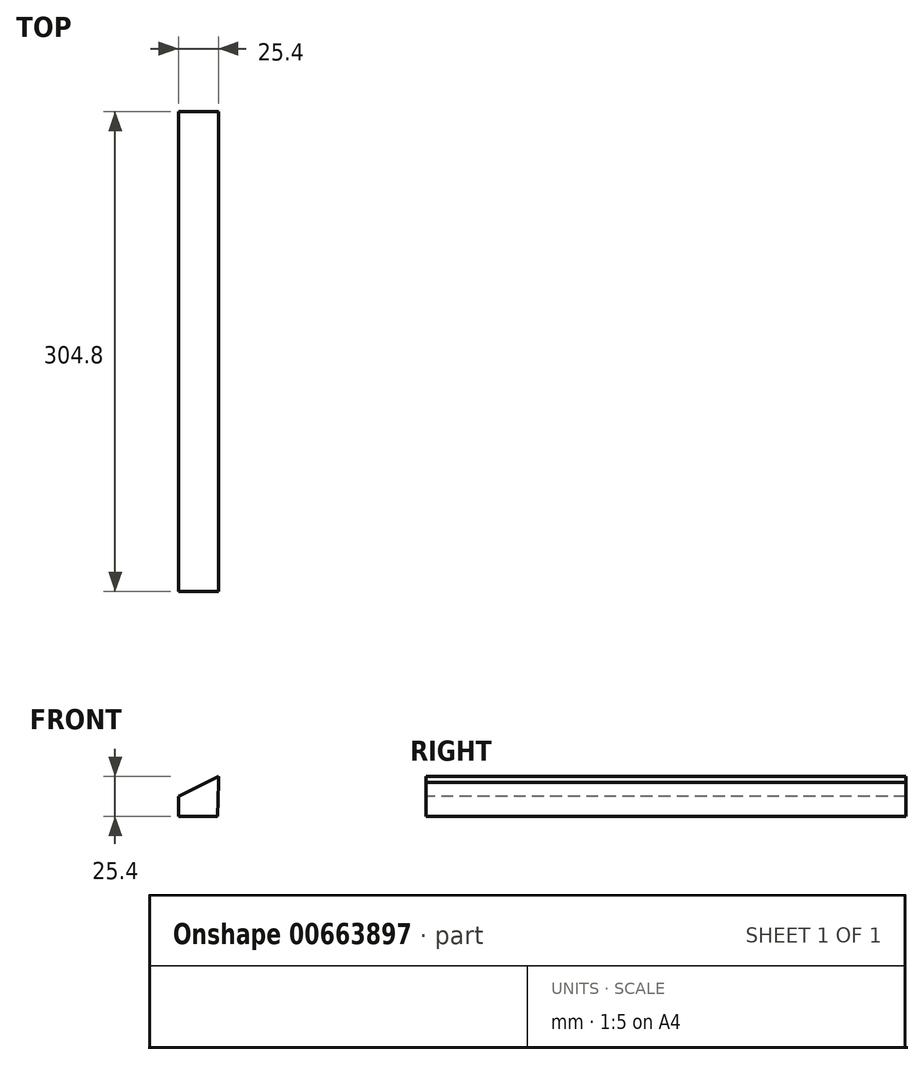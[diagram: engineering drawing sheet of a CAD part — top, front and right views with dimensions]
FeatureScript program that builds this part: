
annotation { "Feature Type Name" : "Feature", "Feature Type Description" : "" }
export const myFeature = defineFeature(function(context is Context, id is Id, definition is map)
    precondition{}
    {
        {
            var Q0;
            Q0=qCreatedBy(makeId("Front.planeOp"),FACE);
            var sketch = newSketch(context, id + "F0", { "sketchPlane" : qUnion([Q0])});
            skLineSegment(sketch, "E0.bottom", {"start": v(-12.7, 12.7) * mm, "end": v(12.7, 12.7) * mm});
            skLineSegment(sketch, "E0.top", {"start": v(-12.7, -12.7) * mm, "end": v(12.7, -12.7) * mm});
            skLineSegment(sketch, "E0.left", {"start": v(-12.7, 12.7) * mm, "end": v(-12.7, -12.7) * mm});
            skLineSegment(sketch, "E0.right", {"start": v(12.7, 12.7) * mm, "end": v(12.7, -12.7) * mm});
            skSolve(sketch);
        }
        {
            var Q0;
            Q0 = qSketchRegion(id + "F0", true);
            extrude(context, id + "F1", {"entities" : qUnion([Q0]), "endBound" : BoundingType.SYMMETRIC, "depth" : 304.8 * mm, "offsetDistance" : 25.4 * mm});
        }
        {
            var Q0;
            Q0=makeQuery(id+"F1.opExtrude","CAP_FACE",FACE,{"disambiguationData":[OSD([sQuery(id+"F0.wireOp",EDGE,"E0.bottom"),sQuery(id+"F0.wireOp",EDGE,"E0.top"),sQuery(id+"F0.wireOp",EDGE,"E0.left"),sQuery(id+"F0.wireOp",EDGE,"E0.right")])],"isStart":false});
            var sketch = newSketch(context, id + "F2", { "sketchPlane" : qUnion([Q0])});
            skLineSegment(sketch, "E1", {"start": v(12.7, 8.9) * mm, "end": v(12.23, -12.7) * mm});
            skLineSegment(sketch, "E2", {"start": v(12.23, -12.7) * mm, "end": v(12.7, -12.7) * mm});
            skLineSegment(sketch, "E3", {"start": v(12.7, -12.7) * mm, "end": v(12.7, 8.9) * mm});
            skLineSegment(sketch, "E4", {"start": v(12.7, 12.7) * mm, "end": v(-12.7, 0) * mm});
            skLineSegment(sketch, "E5", {"start": v(-12.7, 0) * mm, "end": v(-12.7, 12.7) * mm});
            skLineSegment(sketch, "E6", {"start": v(-12.7, 12.7) * mm, "end": v(12.7, 12.7) * mm});
            skSolve(sketch);
        }
        {
            var Q0;
            Q0 = qSketchRegion(id + "F2", true);
            extrude(context, id + "F3", {"entities" : qUnion([Q0]), "operationType" : NewBodyOperationType.REMOVE, "endBound" : BoundingType.THROUGH_ALL, "oppositeDirection" : true, "depth" : 25.4 * mm, "offsetDistance" : 25.4 * mm});
        }
    });
